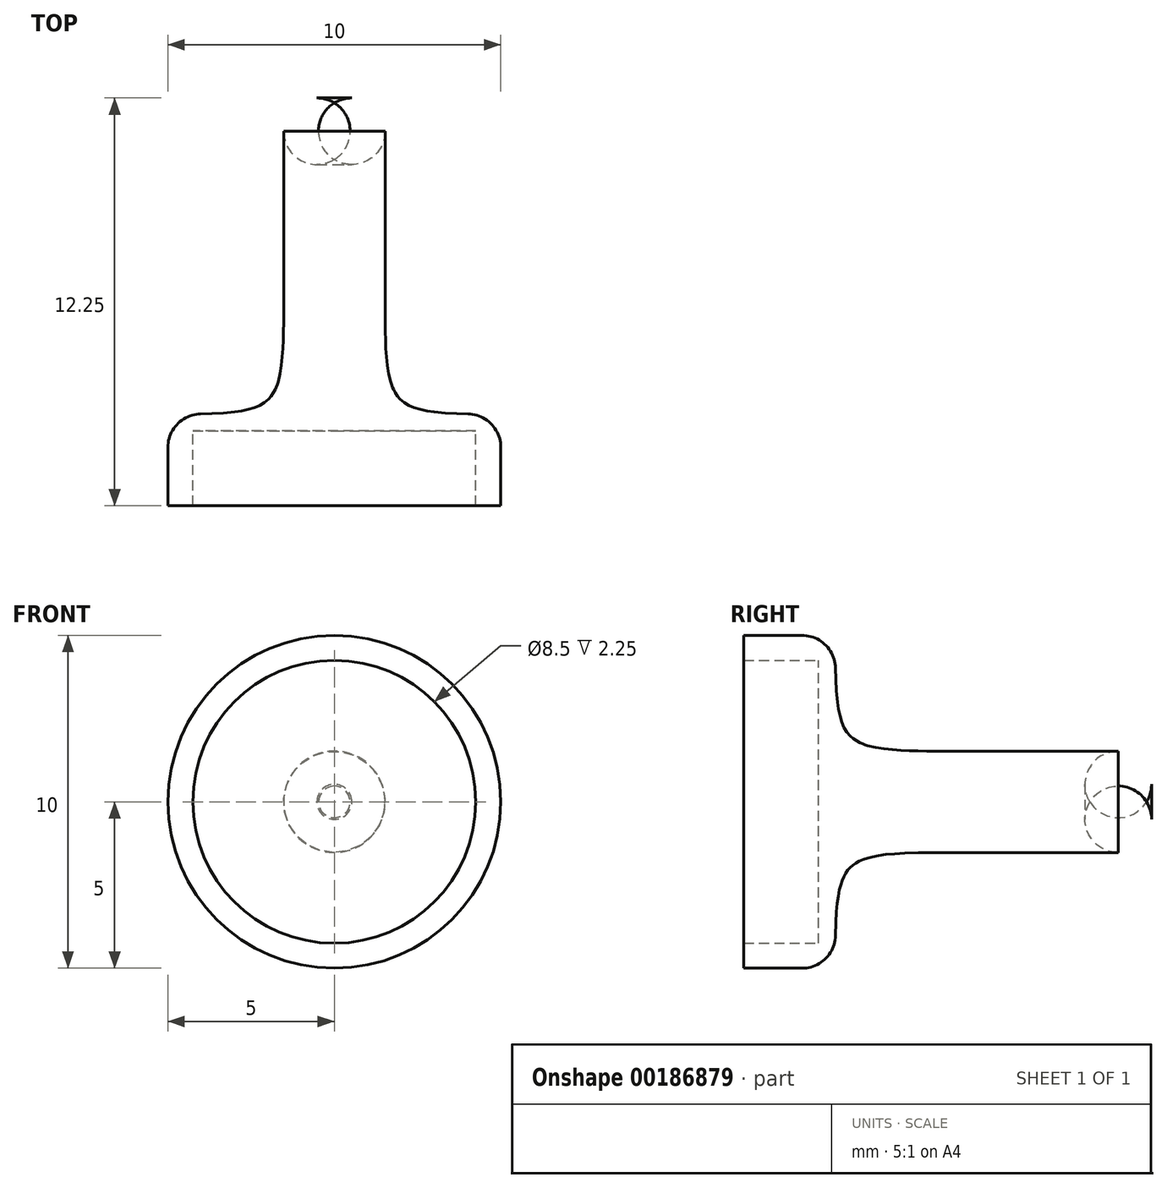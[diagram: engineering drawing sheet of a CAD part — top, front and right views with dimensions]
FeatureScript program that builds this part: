
annotation { "Feature Type Name" : "Feature", "Feature Type Description" : "" }
export const myFeature = defineFeature(function(context is Context, id is Id, definition is map)
    precondition{}
    {
        {
            var Q0;
            Q0=qCreatedBy(makeId("Front.planeOp"),FACE);
            var sketch = newSketch(context, id + "F0", { "sketchPlane" : qUnion([Q0])});
            skCircle(sketch, "E0", {"center": v(0, 0) * mm, "radius": 4.25 * mm});
            skCircle(sketch, "E1", {"center": v(0, 0) * mm, "radius": 5 * mm});
            skSolve(sketch);
        }
        {
            var Q0;
            Q0=makeQuery(id+"F0.imprint","IMPRINT",FACE,{"disambiguationData":[TD([[makeQuery(id+"F0.imprint","IMPRINT",EDGE,{"derivedFrom":sQuery(id+"F0.wireOp",EDGE,"E0")}),-1.0]])]});
            extrude(context, id + "F1", {"entities" : qUnion([Q0]), "depth" : 2.25 * mm});
        }
        {
            var Q0;
            Q0=qCreatedBy(makeId("Front.planeOp"),FACE);
            var sketch = newSketch(context, id + "F2", { "sketchPlane" : qUnion([Q0])});
            skCircle(sketch, "E2", {"center": v(0, 0) * mm, "radius": 5 * mm});
            skSolve(sketch);
        }
        {
            var Q0;
            Q0 = qSketchRegion(id + "F2", true);
            extrude(context, id + "F3", {"entities" : qUnion([Q0]), "operationType" : NewBodyOperationType.ADD, "oppositeDirection" : true, "depth" : 0.5 * mm});
        }
        {
            var Q0;
            Q0=qCreatedBy(makeId("Front.planeOp"),FACE);
            var sketch = newSketch(context, id + "F4", { "sketchPlane" : qUnion([Q0])});
            skCircle(sketch, "E3", {"center": v(0, 0) * mm, "radius": 1.52 * mm});
            skSolve(sketch);
        }
        {
            var Q0;
            Q0=makeQuery(id+"F4.imprint","IMPRINT",FACE,{"disambiguationData":[TD([[makeQuery(id+"F4.imprint","IMPRINT",EDGE,{"derivedFrom":sQuery(id+"F4.wireOp",EDGE,"E3")}),1.0]])]});
            extrude(context, id + "F5", {"entities" : qUnion([Q0]), "operationType" : NewBodyOperationType.ADD, "oppositeDirection" : true, "depth" : 10 * mm});
        }
        {
            var Q0;
            Q0=makeQuery(id+"F5.opExtrude","CAP_FACE",FACE,{"disambiguationData":[OSD([sQuery(id+"F4.wireOp",EDGE,"E3")])],"isStart":false});
            fillet(context, id + "F6", {"entities" : qUnion([Q0]), "radius" : 1 * mm, "tangentPropagation" : true, "allowEdgeOverflow" : false});
        }
        {
            var Q0;
            Q0=makeQuery(id+"F5.boolean.opBoolean","INTERSECT",EDGE,{"derivedFrom":[makeQuery(id+"F3.opExtrude","CAP_FACE",FACE,{"disambiguationData":[OSD([sQuery(id+"F2.wireOp",EDGE,"E2")])],"isStart":false}),makeQuery(id+"F5.opExtrude","SWEPT_FACE",FACE,{"disambiguationData":[OSD([sQuery(id+"F4.wireOp",EDGE,"E3")])]})]});
            fillet(context, id + "F7", {"entities" : qUnion([Q0]), "radius" : 3 * mm, "tangentPropagation" : true, "rho" : 0.7, "crossSection" : FilletCrossSection.CONIC, "allowEdgeOverflow" : false});
        }
        {
            var Q0;
            Q0=makeQuery(id+"F3.opExtrude","CAP_EDGE",EDGE,{"disambiguationData":[OSD([sQuery(id+"F2.wireOp",EDGE,"E2")])],"isStart":false});
            fillet(context, id + "F8", {"entities" : qUnion([Q0]), "radius" : 1 * mm, "tangentPropagation" : true, "allowEdgeOverflow" : false});
        }
    });
